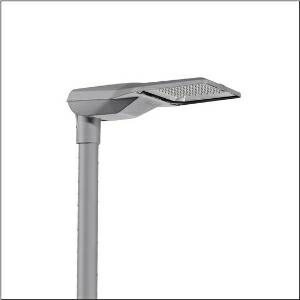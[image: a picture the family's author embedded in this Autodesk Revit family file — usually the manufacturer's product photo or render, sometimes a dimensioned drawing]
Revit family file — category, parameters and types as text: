
# Revit family: streetlight_sl_21_iq_midi___pc-l_5xe3f41g08mb_febf
name_source: partatom
category: Lighting Fixtures
units: mm (PartAtom-declared; Revit-internal decimal feet)

## family parameters
Cut with Voids When Loaded = No
Host = Face
Light Source = No
Part Type = Normal
Room Calculation Point = No
Round Connector Dimension = Use Diameter
Shared = No

## types (1)
- --- (1 x LED, 19370 lm, 146.7 W, 4000K)
    Apparent Load = 147 VA
    CIE Flux Codes = 38 78 98 100 100
    Color Rendering = 70
    Color Temperature = 4000K
    Default Elevation = 1800 mm
    Description = Streetlight SL 21 iQ midi, mast luminaire, primary light control with lens, of PMMA, primary optical cover: cover, of toughened safety glass, transparent, light distribution: PC-L, light emission: direct distribution, primary light characteristic: asymmetric, left, installation type: post-top, side-entry, LED, High Power LED, rated luminous flux: 19.370lm, luminous efficacy: 132lm/W, light colour: 740, colour temperature: 4000K, control gear: iQ Street-Remote, control: Street-Remote, Auto-Match, Temp-Guard, Lumen-Switch, Night-Set, Smart-Wire, Light-Fading, Desk-Remote (wireless, voltage-free reading and setting of iQ features in the workshop via application-optimized NFC function/RFID function), optimised constant luminous flux control (CLO 2.0), pre-setting: linear dimming characteristic, mains connection: 230..240V, AC, 50/60Hz, start of lifetime: 147W, end of service life: 161W, reduction: 62W, luminaire housing, of diecast aluminium, powder-coated, Siteco® metallic grey (DB 702S), corrosivity category C5 mid according to DIN EN ISO 12944, please order mast flange separately, inclination adjustable: 0°, 5°, 10°, 15°, sealing non-destructively replaceable, multi-level sealing system, length: 644mm, width: 335mm, height: 110mm, mast flange for spigot size: 42mm (side-entry): 5XC10008XM4, 60/48mm (side-entry/post-top): 5XC10108XM2, 76/60mm (side-entry/post-top): 5XC10108XM1, mounting height: 4..8m, protection rating (complete): IP66, insulation class (complete): insulation class II (safety insulation), certification: CE, ENEC, ENEC+, VDE, impact resistance: IK10, permissible operating ambient temperature for outdoor applications: -40..+50°C, standard-compliant lighting for roads and squares, packaging unit: 1 piece

Light Distribution: PC-L
    Height = 111 mm
    Lamp = 1 x LED
    Lamp Light Flux = 19370 lm
    Lamp Power = 146.7 W
    Lamp count = 1
    Length = 644 mm
    Luminous efficacy = 132 lm/W
    Manufacturer = Siteco
    ModVariant = No
    Model = 5XE3F41G08MB
    Number of Poles = 1
    OnlyDefault = Yes
    Power Factor = 1
    Product Name = Streetlight SL 21 iQ midi | PC-L
    Product group = mast luminaire | pylon top
    ProductGroupID = 6100
    Protection Class = Protection class II
    Protection Degree = IP 66
    RLX_Detail_Level = 1
    RLX_Emergency_Light_Flux = 0 lm
    RLX_Emergency_Type = 0
    RLX_Emergency_Type_DB = No
    RlxData = <blob elided: 29569 chars, md5=df96d732>
    Socket = socket
    Standby Power = 0 W
    System Light Flux = 19370 lm
    System Power = 147 W
    Type Comments = factory setting: luminous flux: 100 % | dim-lin: 254 | 753 mA
    Type Image = l_1004298.jpg
    URL = http://relux.com
    VarID = @adj_085763
    Voltage = 0 V
    Weight = 0.00 kg
    Width = 336 mm

## geometry (parser evidence)
native form markers: Blend x4, Sweep x10
no freeform markers — native parametric forms only
